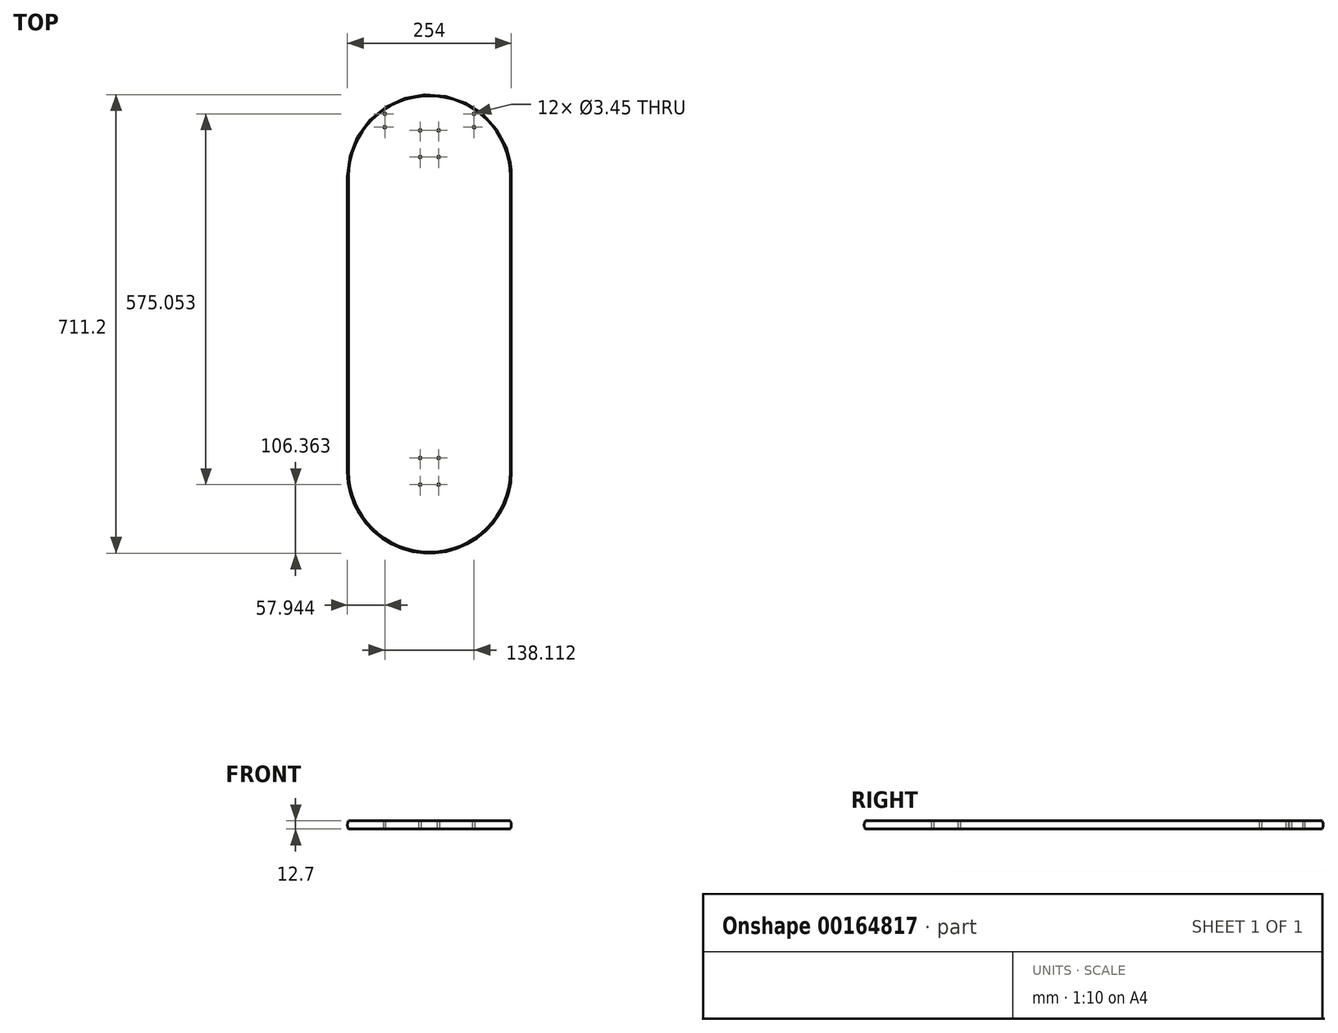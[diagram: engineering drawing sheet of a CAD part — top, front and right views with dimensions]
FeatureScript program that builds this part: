
annotation { "Feature Type Name" : "Feature", "Feature Type Description" : "" }
export const myFeature = defineFeature(function(context is Context, id is Id, definition is map)
    precondition{}
    {
        {
            var Q0;
            Q0=qCreatedBy(makeId("Top.planeOp"),FACE);
            var sketch = newSketch(context, id + "F0", { "sketchPlane" : qUnion([Q0])});
            skLineSegment(sketch, "E0.bottom", {"start": v(0, 0) * mm, "end": v(-254, 0) * mm, "construction": true});
            skLineSegment(sketch, "E0.top", {"start": v(0, -457.2) * mm, "end": v(-254, -457.2) * mm, "construction": true});
            skLineSegment(sketch, "E0.left", {"start": v(0, 0) * mm, "end": v(0, -457.2) * mm});
            skLineSegment(sketch, "E0.right", {"start": v(-254, 0) * mm, "end": v(-254, -457.2) * mm});
            skArc(sketch, "E1", {"start": v(0, 0) * mm, "mid": v(-127, 127) * mm, "end": v(-254, 0) * mm});
            skArc(sketch, "E2", {"start": v(-254, -457.2) * mm, "mid": v(-127, -584.2) * mm, "end": v(0, -457.2) * mm});
            skSolve(sketch);
        }
        {
            var Q0;
            Q0=qSketchRegion(id+"F0",true);
            extrude(context, id + "F1", {"entities" : qUnion([Q0]), "depth" : 12.7 * mm});
        }
        {
            var Q0;
            Q0=makeQuery(id+"F1.opExtrude","CAP_FACE",FACE,{"disambiguationData":[OSD([sQuery(id+"F0.wireOp",EDGE,"E0.top"),sQuery(id+"F0.wireOp",EDGE,"E0.left"),sQuery(id+"F0.wireOp",EDGE,"E0.right"),sQuery(id+"F0.wireOp",EDGE,"SqmiRByB-BWnK-mEMi-qFd4-4WnWEakNxxXd"),sQuery(id+"F0.wireOp",EDGE,"jWmXs5kq-5ELT-ZpDA-D124-8Izf0WwcNPap")])],"isStart":false});
            var sketch = newSketch(context, id + "F2", { "sketchPlane" : qUnion([Q0])});
            skLineSegment(sketch, "E3.bottom", {"start": v(-196.06, 97.22) * mm, "end": v(-57.94, 97.22) * mm, "construction": true});
            skLineSegment(sketch, "E3.top", {"start": v(-196.06, 76.58) * mm, "end": v(-57.94, 76.58) * mm, "construction": true});
            skLineSegment(sketch, "E3.left", {"start": v(-196.06, 97.22) * mm, "end": v(-196.06, 76.58) * mm, "construction": true});
            skLineSegment(sketch, "E3.right", {"start": v(-57.94, 97.22) * mm, "end": v(-57.94, 76.58) * mm, "construction": true});
            skLineSegment(sketch, "E4", {"start": v(-57.94, 97.22) * mm, "end": v(-52.39, 97.22) * mm, "construction": true});
            skLineSegment(sketch, "E5", {"start": v(-52.39, 97.22) * mm, "end": v(-52.39, 102.77) * mm, "construction": true});
            skCircle(sketch, "E6", {"center": v(-57.94, 97.22) * mm, "radius": 1.73 * mm});
            skCircle(sketch, "E7", {"center": v(-57.94, 76.58) * mm, "radius": 1.73 * mm});
            skCircle(sketch, "E8", {"center": v(-196.06, 76.58) * mm, "radius": 1.73 * mm});
            skCircle(sketch, "E9", {"center": v(-196.06, 97.22) * mm, "radius": 1.73 * mm});
            skLineSegment(sketch, "E10", {"start": v(-127, 97.22) * mm, "end": v(-127, 127) * mm, "construction": true});
            skSolve(sketch);
        }
        {
            var Q0;
            Q0=qSketchRegion(id+"F2",true);
            var Q1;
            Q1=makeQuery(id+"F1.opExtrude","CAP_FACE",FACE,{"disambiguationData":[OSD([sQuery(id+"F0.wireOp",EDGE,"E0.top"),sQuery(id+"F0.wireOp",EDGE,"E0.left"),sQuery(id+"F0.wireOp",EDGE,"E0.right"),sQuery(id+"F0.wireOp",EDGE,"SqmiRByB-BWnK-mEMi-qFd4-4WnWEakNxxXd"),sQuery(id+"F0.wireOp",EDGE,"jWmXs5kq-5ELT-ZpDA-D124-8Izf0WwcNPap")])],"isStart":true});
            extrude(context, id + "F3", {"entities" : qUnion([Q0]), "operationType" : NewBodyOperationType.REMOVE, "endBound" : BoundingType.UP_TO_SURFACE, "oppositeDirection" : true, "endBoundEntityFace" : qUnion([Q1]), "depth" : 25.4 * mm});
        }
        {
            var Q0;
            Q0=makeQuery(id+"F1.opExtrude","CAP_FACE",FACE,{"disambiguationData":[OSD([sQuery(id+"F0.wireOp",EDGE,"E0.left"),sQuery(id+"F0.wireOp",EDGE,"E0.right"),sQuery(id+"F0.wireOp",EDGE,"E1"),sQuery(id+"F0.wireOp",EDGE,"E2")])],"isStart":false});
            var sketch = newSketch(context, id + "F4", { "sketchPlane" : qUnion([Q0])});
            skLineSegment(sketch, "E11", {"start": v(-127, 50.8) * mm, "end": v(-127, -457.2) * mm, "construction": true});
            skLineSegment(sketch, "E12.bottom", {"start": v(-112.71, 30.16) * mm, "end": v(-141.29, 30.16) * mm, "construction": true});
            skLineSegment(sketch, "E12.top", {"start": v(-112.71, 71.44) * mm, "end": v(-141.29, 71.44) * mm, "construction": true});
            skLineSegment(sketch, "E12.left", {"start": v(-112.71, 30.16) * mm, "end": v(-112.71, 71.44) * mm, "construction": true});
            skLineSegment(sketch, "E12.right", {"start": v(-141.29, 30.16) * mm, "end": v(-141.29, 71.44) * mm, "construction": true});
            skPoint(sketch, "E12.middle", {"position": v(-127, 50.8) * mm});
            skLineSegment(sketch, "E13.bottom", {"start": v(-112.71, -477.84) * mm, "end": v(-141.29, -477.84) * mm, "construction": true});
            skLineSegment(sketch, "E13.top", {"start": v(-112.71, -436.56) * mm, "end": v(-141.29, -436.56) * mm, "construction": true});
            skLineSegment(sketch, "E13.left", {"start": v(-112.71, -477.84) * mm, "end": v(-112.71, -436.56) * mm, "construction": true});
            skLineSegment(sketch, "E13.right", {"start": v(-141.29, -477.84) * mm, "end": v(-141.29, -436.56) * mm, "construction": true});
            skPoint(sketch, "E13.middle", {"position": v(-127, -457.2) * mm});
            skLineSegment(sketch, "E14", {"start": v(-127, 50.8) * mm, "end": v(-127, 127) * mm, "construction": true});
            skCircle(sketch, "E15", {"center": v(-112.71, 71.44) * mm, "radius": 1.73 * mm});
            skCircle(sketch, "E16", {"center": v(-112.71, 30.16) * mm, "radius": 1.73 * mm});
            skCircle(sketch, "E17", {"center": v(-141.29, 30.16) * mm, "radius": 1.73 * mm});
            skCircle(sketch, "E18", {"center": v(-141.29, 71.44) * mm, "radius": 1.73 * mm});
            skCircle(sketch, "E19", {"center": v(-141.29, -436.56) * mm, "radius": 1.73 * mm});
            skCircle(sketch, "E20", {"center": v(-112.71, -436.56) * mm, "radius": 1.73 * mm});
            skCircle(sketch, "E21", {"center": v(-112.71, -477.84) * mm, "radius": 1.73 * mm});
            skCircle(sketch, "E22", {"center": v(-141.29, -477.84) * mm, "radius": 1.73 * mm});
            skSolve(sketch);
        }
        {
            var Q0;
            Q0 = qSketchRegion(id + "F4", true);
            var Q1;
            Q1=makeQuery(id+"F1.opExtrude","CAP_FACE",FACE,{"disambiguationData":[OSD([sQuery(id+"F0.wireOp",EDGE,"E0.left"),sQuery(id+"F0.wireOp",EDGE,"E0.right"),sQuery(id+"F0.wireOp",EDGE,"E1"),sQuery(id+"F0.wireOp",EDGE,"E2")])],"isStart":true});
            extrude(context, id + "F5", {"entities" : qUnion([Q0]), "operationType" : NewBodyOperationType.REMOVE, "endBound" : BoundingType.UP_TO_SURFACE, "oppositeDirection" : true, "endBoundEntityFace" : qUnion([Q1]), "depth" : 25.4 * mm});
        }
        {
            var Q0;
            Q0=qCreatedBy(makeId("Front.planeOp"),FACE);
            var sketch = newSketch(context, id + "F6", { "sketchPlane" : qUnion([Q0])});
            skLineSegment(sketch, "E23.bottom", {"start": v(0, 0) * mm, "end": v(-1.7, 0) * mm});
            skLineSegment(sketch, "E23.top", {"start": v(0, 12.7) * mm, "end": v(-1.7, 12.7) * mm});
            skLineSegment(sketch, "E23.left", {"start": v(0, 0) * mm, "end": v(0, 12.7) * mm});
            skLineSegment(sketch, "E23.right", {"start": v(-1.7, 0) * mm, "end": v(-1.7, 12.7) * mm, "construction": true});
            skArc(sketch, "E24", {"start": v(-1.7, 0) * mm, "mid": v(0, 6.35) * mm, "end": v(-1.7, 12.7) * mm});
            skSolve(sketch);
        }
        {
            var Q0;
            Q0 = qSketchRegion(id + "F6", true);
            var Q1;
            Q1=makeQuery(id+"F1.opExtrude","CAP_EDGE",EDGE,{"disambiguationData":[OSD([sQuery(id+"F0.wireOp",EDGE,"E1")])],"isStart":false});
            var Q2;
            Q2=makeQuery(id+"F1.opExtrude","CAP_EDGE",EDGE,{"disambiguationData":[OSD([sQuery(id+"F0.wireOp",EDGE,"E0.right")])],"isStart":false});
            var Q3;
            Q3=makeQuery(id+"F1.opExtrude","CAP_EDGE",EDGE,{"disambiguationData":[OSD([sQuery(id+"F0.wireOp",EDGE,"E2")])],"isStart":false});
            var Q4;
            Q4=makeQuery(id+"F1.opExtrude","CAP_EDGE",EDGE,{"disambiguationData":[OSD([sQuery(id+"F0.wireOp",EDGE,"E0.left")])],"isStart":false});
            sweep(context, id + "F7", {"operationType" : NewBodyOperationType.REMOVE, "profiles" : qUnion([Q0]), "path" : qUnion([Q1, Q2, Q3, Q4])});
        }
    });
